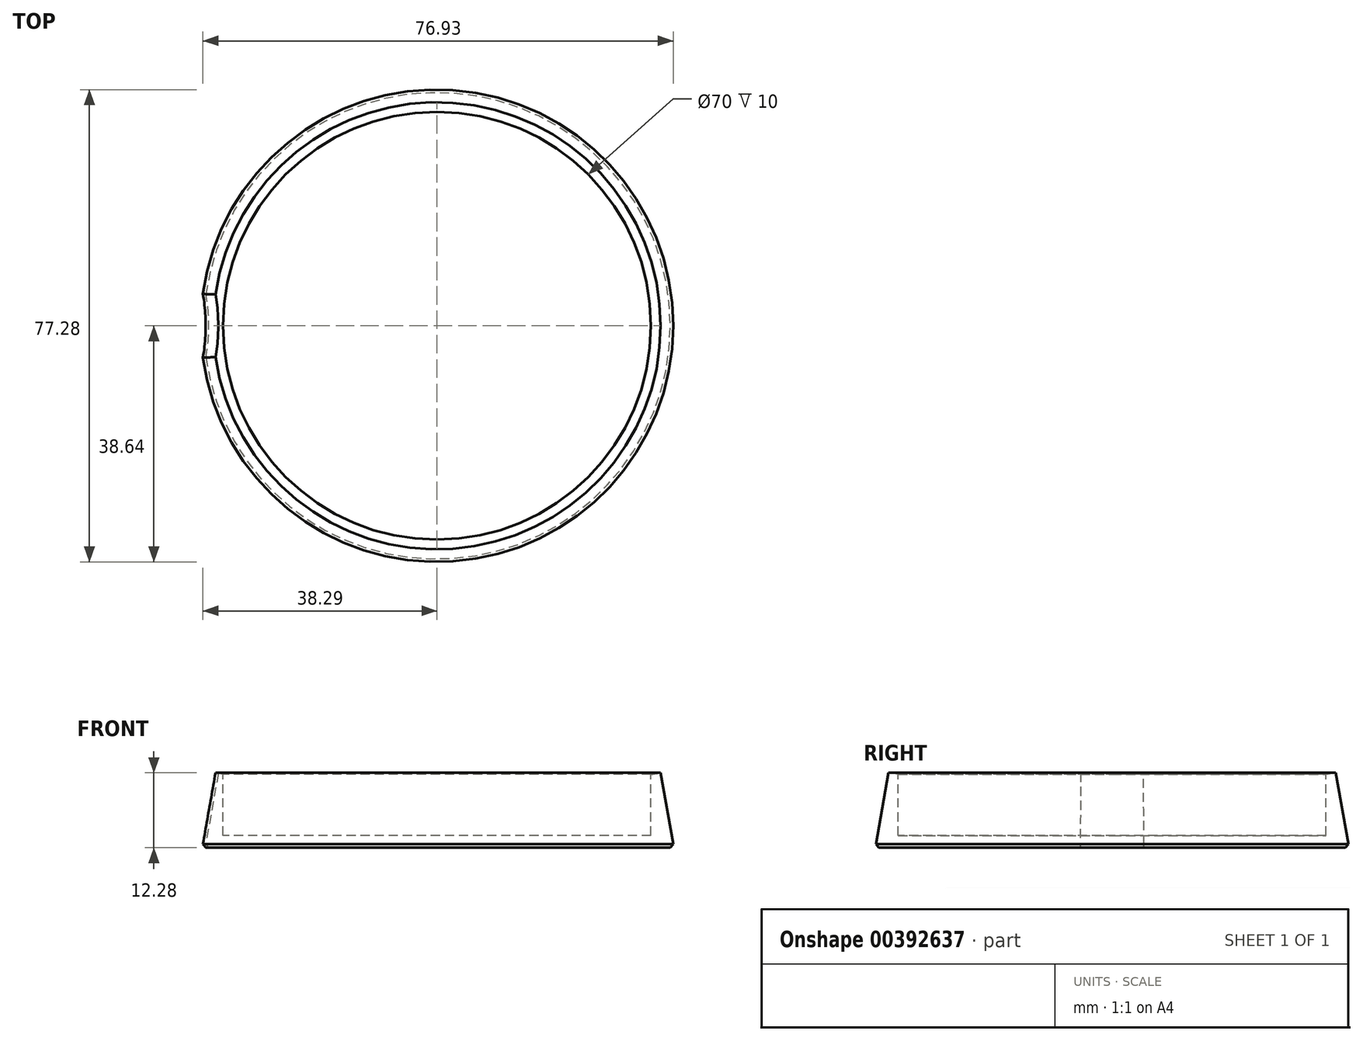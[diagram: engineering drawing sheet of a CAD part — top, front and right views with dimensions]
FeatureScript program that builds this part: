
annotation { "Feature Type Name" : "Feature", "Feature Type Description" : "" }
export const myFeature = defineFeature(function(context is Context, id is Id, definition is map)
    precondition{}
    {
        {
            var Q0;
            Q0=qCreatedBy(makeId("Front.planeOp"),FACE);
            var sketch = newSketch(context, id + "F0", { "sketchPlane" : qUnion([Q0])});
            skLineSegment(sketch, "E0", {"start": v(0, 0) * mm, "end": v(-38.74, 0) * mm});
            skLineSegment(sketch, "E1", {"start": v(-38.74, 0) * mm, "end": v(-36.58, 12.28) * mm});
            skLineSegment(sketch, "E2", {"start": v(-36.58, 12.28) * mm, "end": v(-35, 12) * mm});
            skLineSegment(sketch, "E3", {"start": v(-35, 12) * mm, "end": v(-35, 2) * mm});
            skLineSegment(sketch, "E4", {"start": v(-35, 2) * mm, "end": v(0, 2) * mm});
            skLineSegment(sketch, "E5", {"start": v(0, 2) * mm, "end": v(0, 0) * mm});
            skSolve(sketch);
        }
        {
            var Q0;
            Q0=makeQuery(id+"F0.imprint","IMPRINT",FACE,{"disambiguationData":[TD([[makeQuery(id+"F0.imprint","IMPRINT",EDGE,{"derivedFrom":sQuery(id+"F0.wireOp",EDGE,"E0")}),-1.0]])]});
            var Q1;
            Q1=sQuery(id+"F0.wireOp",EDGE,"E5");
            revolve(context, id + "F1", {"entities" : qUnion([Q0]), "axis" : qUnion([Q1]), "revolveType" : RevolveType.FULL});
        }
        {
            var Q0;
            Q0=qCreatedBy(makeId("Front.planeOp"),FACE);
            var sketch = newSketch(context, id + "F2", { "sketchPlane" : qUnion([Q0])});
            skLineSegment(sketch, "E6", {"start": v(-62.94, 30.89) * mm, "end": v(-68.61, -1.27) * mm});
            skLineSegment(sketch, "E7", {"start": v(-68.61, -1.27) * mm, "end": v(-39.07, -6.48) * mm});
            skLineSegment(sketch, "E8", {"start": v(-39.07, -6.48) * mm, "end": v(-33.4, 25.68) * mm});
            skLineSegment(sketch, "E9", {"start": v(-33.4, 25.68) * mm, "end": v(-62.94, 30.89) * mm});
            skSolve(sketch);
        }
        {
            var Q0;
            Q0=makeQuery(id+"F2.imprint","IMPRINT",FACE,{"disambiguationData":[TD([[makeQuery(id+"F2.imprint","IMPRINT",EDGE,{"derivedFrom":sQuery(id+"F2.wireOp",EDGE,"E6")}),1.0]])]});
            var Q1;
            Q1=sQuery(id+"F2.wireOp",EDGE,"E6");
            revolve(context, id + "F3", {"operationType" : NewBodyOperationType.REMOVE, "entities" : qUnion([Q0]), "axis" : qUnion([Q1]), "revolveType" : RevolveType.FULL, "oppositeDirection" : true});
        }
        {
            var Q0;
            Q0=makeQuery(id+"F1.opRevolve","SWEPT_FACE",FACE,{"disambiguationData":[OSD([sQuery(id+"F0.wireOp",EDGE,"E0")])]});
            chamfer(context, id + "F4", {"entities" : qUnion([Q0]), "width" : .5 * mm, "tangentPropagation" : true});
        }
    });
